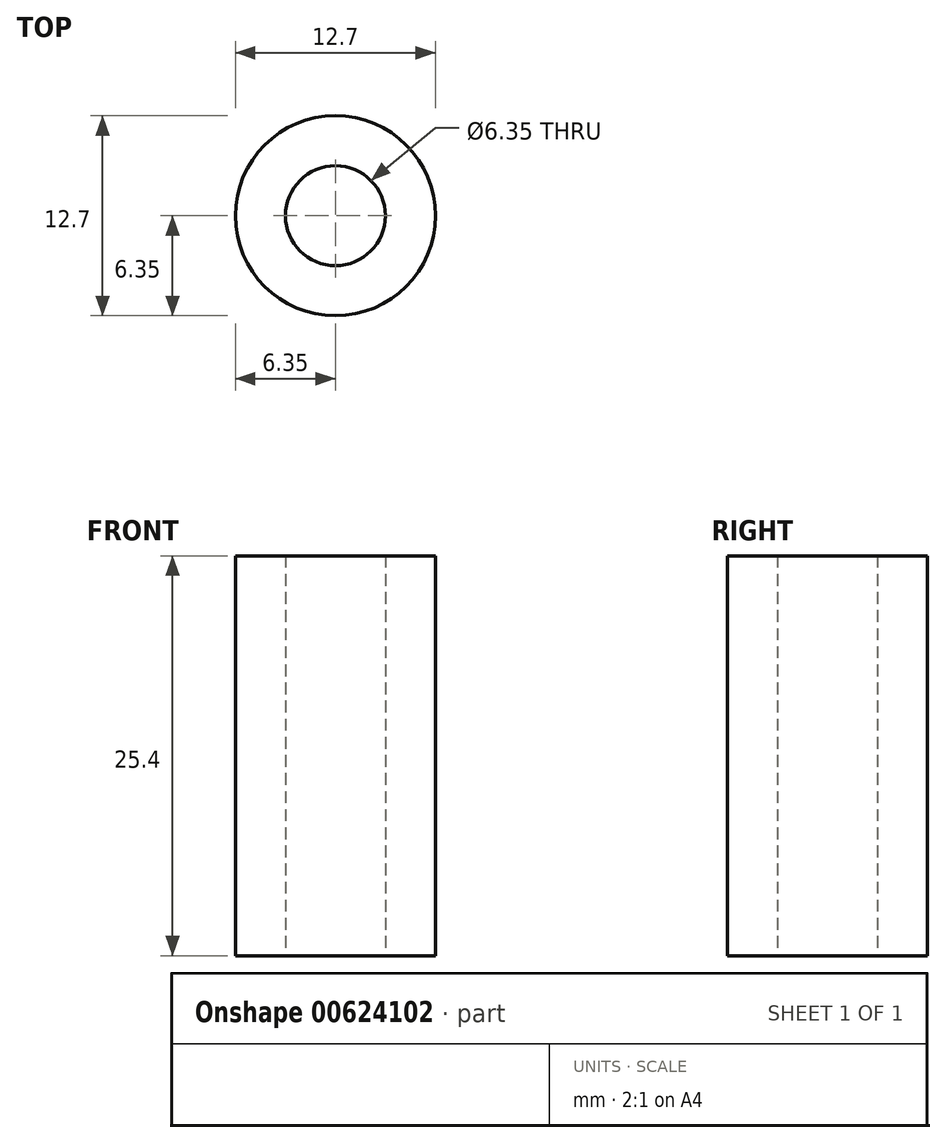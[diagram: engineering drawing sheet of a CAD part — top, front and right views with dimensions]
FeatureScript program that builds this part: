
annotation { "Feature Type Name" : "Feature", "Feature Type Description" : "" }
export const myFeature = defineFeature(function(context is Context, id is Id, definition is map)
    precondition{}
    {
        {
            var Q0;
            Q0=qCreatedBy(makeId("Top.planeOp"),FACE);
            var sketch = newSketch(context, id + "F0", { "sketchPlane" : qUnion([Q0])});
            skCircle(sketch, "E0", {"center": v(0, 0) * mm, "radius": 6.35 * mm});
            skCircle(sketch, "E1", {"center": v(0, 0) * mm, "radius": 3.18 * mm});
            skSolve(sketch);
        }
        {
            var Q0;
            Q0=makeQuery(id+"F0.imprint","IMPRINT",FACE,{"disambiguationData":[TD([[makeQuery(id+"F0.imprint","IMPRINT",EDGE,{"derivedFrom":sQuery(id+"F0.wireOp",EDGE,"E0")}),1.0]])]});
            extrude(context, id + "F1", {"entities" : qUnion([Q0]), "depth" : 25.4 * mm, "offsetDistance" : 25.4 * mm});
        }
    });
